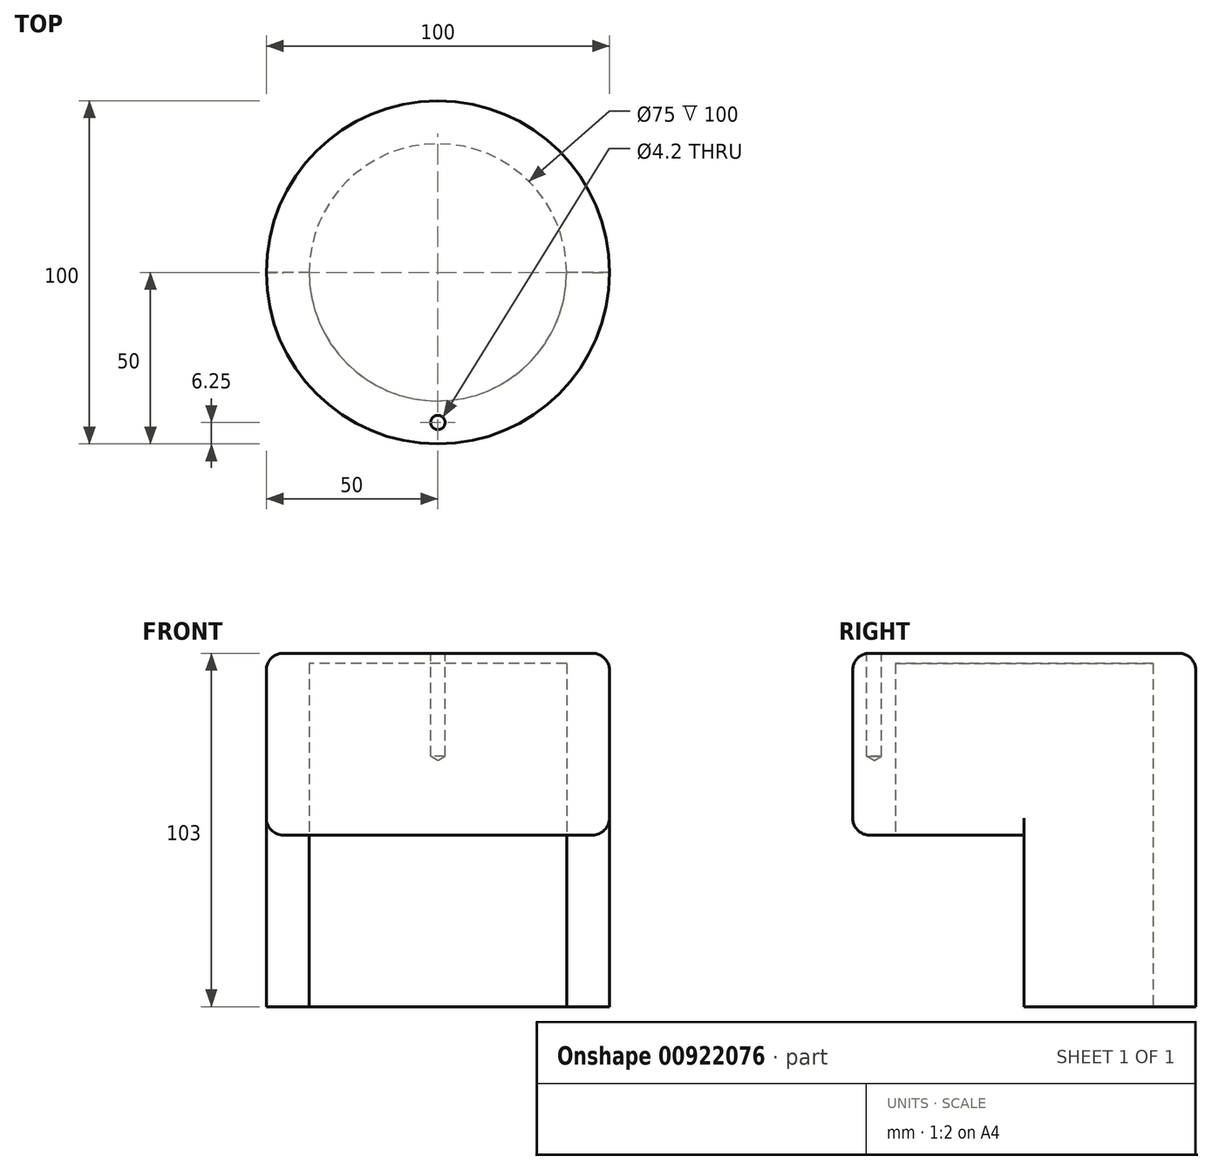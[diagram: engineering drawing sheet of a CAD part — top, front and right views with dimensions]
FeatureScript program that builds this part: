
annotation { "Feature Type Name" : "Feature", "Feature Type Description" : "" }
export const myFeature = defineFeature(function(context is Context, id is Id, definition is map)
    precondition{}
    {
        {
            var Q0;
            Q0=qCreatedBy(makeId("Top.planeOp"),FACE);
            var sketch = newSketch(context, id + "F0", { "sketchPlane" : qUnion([Q0])});
            skCircle(sketch, "E0", {"center": v(0, 0) * mm, "radius": 50 * mm});
            skCircle(sketch, "E1", {"center": v(0, 0) * mm, "radius": 37.5 * mm});
            skSolve(sketch);
        }
        {
            var Q0;
            Q0 = qSketchRegion(id + "F0", true);
            extrude(context, id + "F1", {"entities" : qUnion([Q0]), "depth" : 100 * mm, "offsetDistance" : 25 * mm});
        }
        {
            var Q0;
            Q0=qCreatedBy(makeId("Front.planeOp"),FACE);
            var sketch = newSketch(context, id + "F2", { "sketchPlane" : qUnion([Q0])});
            skLineSegment(sketch, "E2.bottom", {"start": v(155.29, 0) * mm, "end": v(-143.72, 0) * mm});
            skLineSegment(sketch, "E2.top", {"start": v(155.29, 50) * mm, "end": v(-143.72, 50) * mm});
            skLineSegment(sketch, "E2.left", {"start": v(155.29, 0) * mm, "end": v(155.29, 50) * mm});
            skLineSegment(sketch, "E2.right", {"start": v(-143.72, 0) * mm, "end": v(-143.72, 50) * mm});
            skSolve(sketch);
        }
        {
            var Q0;
            Q0=makeQuery(id+"F2.imprint","IMPRINT",FACE,{"disambiguationData":[TD([[makeQuery(id+"F2.imprint","IMPRINT",EDGE,{"derivedFrom":sQuery(id+"F2.wireOp",EDGE,"E2.bottom")}),-1.0]])]});
            extrude(context, id + "F3", {"entities" : qUnion([Q0]), "operationType" : NewBodyOperationType.REMOVE, "endBound" : BoundingType.THROUGH_ALL, "depth" : 25 * mm, "offsetDistance" : 25 * mm});
        }
        {
            var Q0;
            Q0=makeQuery(id+"F1.opExtrude","CAP_FACE",FACE,{"disambiguationData":[OSD([sQuery(id+"F0.wireOp",EDGE,"E0"),sQuery(id+"F0.wireOp",EDGE,"E1")])],"isStart":false});
            var sketch = newSketch(context, id + "F4", { "sketchPlane" : qUnion([Q0])});
            skCircle(sketch, "E3", {"center": v(0, 0) * mm, "radius": 50 * mm});
            skSolve(sketch);
        }
        {
            var Q0;
            Q0 = qSketchRegion(id + "F4", true);
            extrude(context, id + "F5", {"entities" : qUnion([Q0]), "operationType" : NewBodyOperationType.ADD, "depth" : 3 * mm, "offsetDistance" : 25 * mm});
        }
        {
            var Q0;
            Q0=makeQuery(id+"F3.boolean.opBoolean","INTERSECT",EDGE,{"derivedFrom":[makeQuery(id+"F1.opExtrude","SWEPT_FACE",FACE,{"disambiguationData":[OSD([sQuery(id+"F0.wireOp",EDGE,"E0")])]}),makeQuery(id+"F3.opExtrude","SWEPT_FACE",FACE,{"disambiguationData":[OSD([sQuery(id+"F2.wireOp",EDGE,"E2.top")])]})]});
            fillet(context, id + "F6", {"entities" : qUnion([Q0]), "radius" : 5 * mm, "tangentPropagation" : true, "allowEdgeOverflow" : false});
        }
        {
            var Q0;
            Q0=makeQuery(id+"F5.opExtrude","CAP_EDGE",EDGE,{"disambiguationData":[OSD([sQuery(id+"F4.wireOp",EDGE,"E3")])],"isStart":false});
            fillet(context, id + "F7", {"entities" : qUnion([Q0]), "radius" : 5 * mm, "tangentPropagation" : true, "allowEdgeOverflow" : false});
        }
        {
            var Q0;
            Q0=makeQuery(id+"F5.opExtrude","CAP_FACE",FACE,{"disambiguationData":[OSD([sQuery(id+"F4.wireOp",EDGE,"E3")])],"isStart":false});
            var sketch = newSketch(context, id + "F8", { "sketchPlane" : qUnion([Q0])});
            skCircle(sketch, "E4", {"center": v(0, 0) * mm, "radius": 43.75 * mm});
            skPoint(sketch, "E5", {"position": v(0, -43.75) * mm});
            skSolve(sketch);
        }
        {
            var Q0;
            Q0=sQuery(id+"F8.wireOp",VERTEX,"E5");
            var Q1;
            Q1=makeQuery(id+"F1.opExtrude","SWEPT_BODY",BODY,{"disambiguationData":[OSD([sQuery(id+"F0.wireOp",EDGE,"E0"),sQuery(id+"F0.wireOp",EDGE,"E1")])]});
            hole(context, id + "F9", {"style" : HoleStyle.SIMPLE, "endStyle" : HoleEndStyle.BLIND, "standardTappedOrClearance" : lookupTablePath({ "standard" : "ISO", "engagement" : "75%", "pitch" : "0.8 mm", "size" : "M5", "type" : "Tapped" }), "standardBlindInLast" : lookupTablePath({ "standard" : "ISO", "engagement" : "75%", "pitch" : "0.8 mm", "size" : "M5", "type" : "Tapped" }), "holeDiameter" : 4.2 * mm, "majorDiameter" : 5 * mm, "showTappedDepth" : true, "holeDepth" : 30 * mm, "isTappedThrough" : true, "tappedDepth" : 27.6 * mm, "tapClearance" : 3, "startFromSketch" : true, "locations" : qUnion([Q0]), "scope" : qUnion([Q1])});
        }
    });
